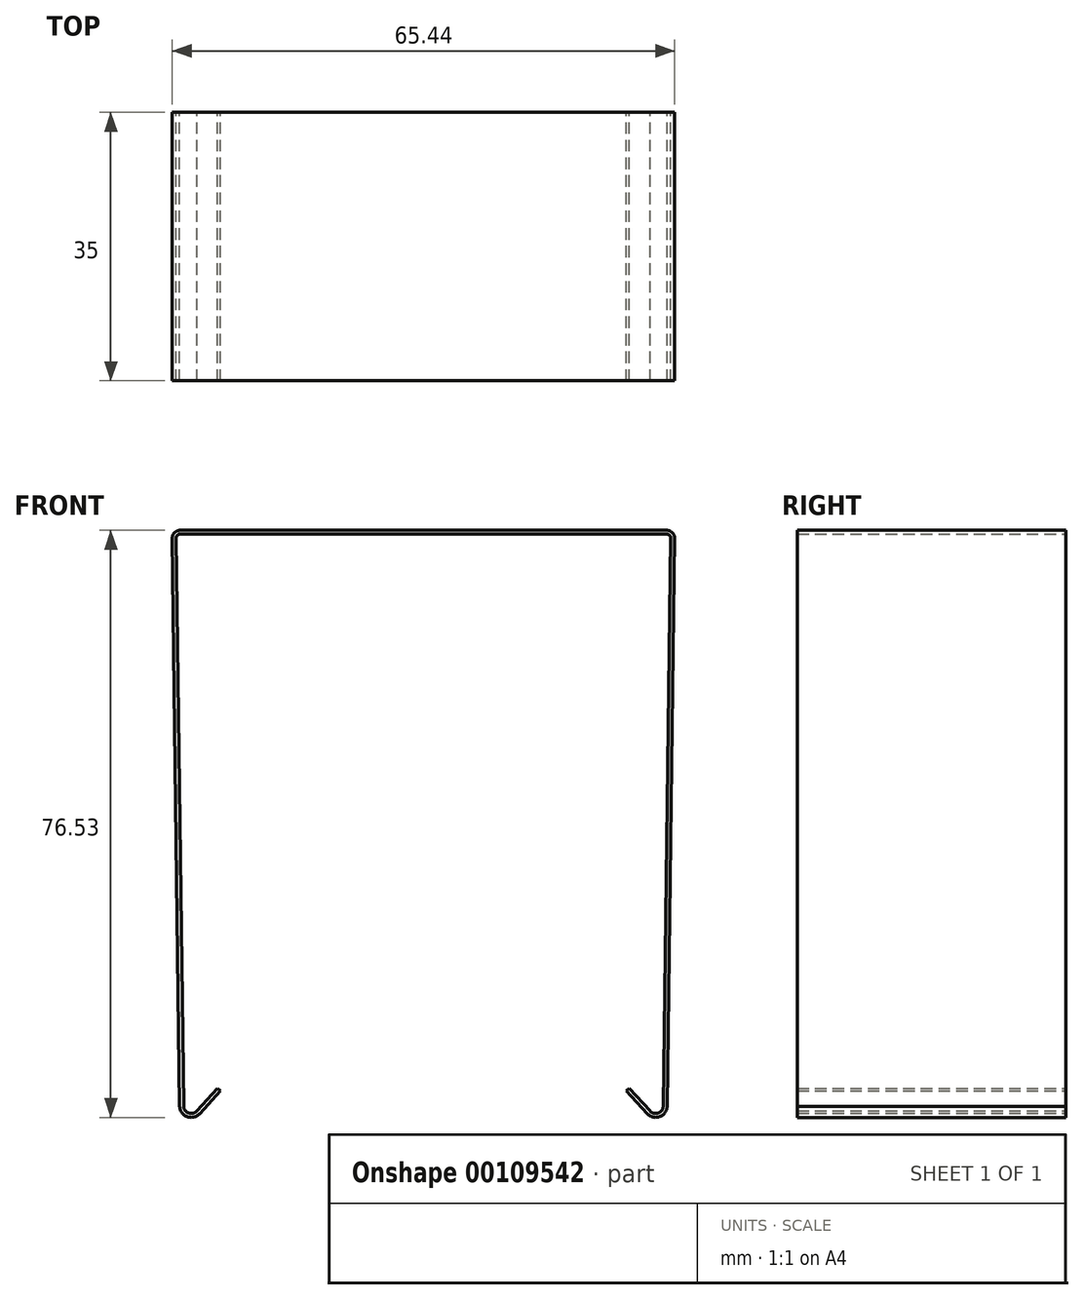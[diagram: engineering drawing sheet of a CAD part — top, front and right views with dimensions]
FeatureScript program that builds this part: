
annotation { "Feature Type Name" : "Feature", "Feature Type Description" : "" }
export const myFeature = defineFeature(function(context is Context, id is Id, definition is map)
    precondition{}
    {
        {
            var Q0;
            Q0=qCreatedBy(makeId("Front.planeOp"),FACE);
            var sketch = newSketch(context, id + "F0", { "sketchPlane" : qUnion([Q0])});
            skLineSegment(sketch, "E0", {"start": v(0, 0) * mm, "end": v(12.09, 0) * mm});
            skLineSegment(sketch, "E1", {"start": v(32.7, -3.05) * mm, "end": v(31.76, -75.1) * mm});
            skLineSegment(sketch, "E2", {"start": v(26.47, -73.06) * mm, "end": v(29.15, -76.03) * mm});
            skArc(sketch, "E3", {"start": v(29.15, -76.03) * mm, "mid": v(30.77, -76.44) * mm, "end": v(31.76, -75.1) * mm});
            skLineSegment(sketch, "E4", {"start": v(26.47, -73.06) * mm, "end": v(26.84, -72.73) * mm});
            skLineSegment(sketch, "E5", {"start": v(26.84, -72.73) * mm, "end": v(29.52, -75.7) * mm});
            skLineSegment(sketch, "E6", {"start": v(31.25, -75.03) * mm, "end": v(32.2, -3.03) * mm});
            skArc(sketch, "E7", {"start": v(29.52, -75.7) * mm, "mid": v(30.61, -75.94) * mm, "end": v(31.25, -75.03) * mm});
            skLineSegment(sketch, "E8", {"start": v(0, 0) * mm, "end": v(0, -0.5) * mm});
            skLineSegment(sketch, "E9", {"start": v(12.09, -0.5) * mm, "end": v(0, -0.5) * mm});
            skLineSegment(sketch, "E10", {"start": v(32.2, -3.03) * mm, "end": v(40.94, -3.03) * mm, "construction": true});
            skLineSegment(sketch, "E11", {"start": v(31.25, -75.03) * mm, "end": v(43.25, -75.03) * mm, "construction": true});
            skLineSegment(sketch, "E12", {"start": v(12.09, 0) * mm, "end": v(31.72, 0) * mm});
            skLineSegment(sketch, "E13", {"start": v(32.7, -3.05) * mm, "end": v(32.72, -1.01) * mm});
            skPoint(sketch, "E14.visualSharp", {"position": v(32.74, 0) * mm});
            skArc(sketch, "E14.filletArc", {"start": v(32.72, -1.01) * mm, "mid": v(32.44, -0.3) * mm, "end": v(31.72, 0) * mm});
            skLineSegment(sketch, "E15", {"start": v(12.09, -0.5) * mm, "end": v(31.72, -0.5) * mm});
            skLineSegment(sketch, "E16", {"start": v(32.2, -3.03) * mm, "end": v(32.22, -1) * mm});
            skPoint(sketch, "E17.visualSharp", {"position": v(32.23, -0.5) * mm});
            skArc(sketch, "E17.filletArc", {"start": v(32.22, -1) * mm, "mid": v(32.08, -0.65) * mm, "end": v(31.72, -0.5) * mm});
            skArc(sketch, "E18.MirrorCS", {"start": v(-29.15, -76.03) * mm, "mid": v(-30.77, -76.44) * mm, "end": v(-31.76, -75.1) * mm});
            skArc(sketch, "E19.MirrorCS", {"start": v(-29.52, -75.7) * mm, "mid": v(-30.61, -75.94) * mm, "end": v(-31.25, -75.03) * mm});
            skArc(sketch, "E20.MirrorCS", {"start": v(-32.72, -1.01) * mm, "mid": v(-32.44, -0.3) * mm, "end": v(-31.72, 0) * mm});
            skLineSegment(sketch, "E21.MirrorCS", {"start": v(-26.47, -73.06) * mm, "end": v(-26.84, -72.73) * mm});
            skArc(sketch, "E22.MirrorCS", {"start": v(-32.22, -1) * mm, "mid": v(-32.08, -0.65) * mm, "end": v(-31.72, -0.5) * mm});
            skLineSegment(sketch, "E23.MirrorCS", {"start": v(-32.7, -3.05) * mm, "end": v(-32.72, -1.01) * mm});
            skLineSegment(sketch, "E24.MirrorCS", {"start": v(-32.2, -3.03) * mm, "end": v(-32.22, -1) * mm});
            skLineSegment(sketch, "E25.MirrorCS", {"start": v(-26.47, -73.06) * mm, "end": v(-29.15, -76.03) * mm});
            skLineSegment(sketch, "E26.MirrorCS", {"start": v(-26.84, -72.73) * mm, "end": v(-29.52, -75.7) * mm});
            skLineSegment(sketch, "E27.MirrorCS", {"start": v(0, 0) * mm, "end": v(-12.09, 0) * mm});
            skLineSegment(sketch, "E28.MirrorCS", {"start": v(-12.09, 0) * mm, "end": v(-31.72, 0) * mm});
            skLineSegment(sketch, "E29.MirrorCS", {"start": v(-12.09, -0.5) * mm, "end": v(0, -0.5) * mm});
            skLineSegment(sketch, "E30.MirrorCS", {"start": v(-31.25, -75.03) * mm, "end": v(-43.25, -75.03) * mm, "construction": true});
            skLineSegment(sketch, "E31.MirrorCS", {"start": v(-32.2, -3.03) * mm, "end": v(-40.94, -3.03) * mm, "construction": true});
            skLineSegment(sketch, "E32.MirrorCS", {"start": v(-12.09, -0.5) * mm, "end": v(-31.72, -0.5) * mm});
            skPoint(sketch, "E33.MirrorP", {"position": v(-32.23, -0.5) * mm});
            skLineSegment(sketch, "E34.MirrorCS", {"start": v(-32.7, -3.05) * mm, "end": v(-31.76, -75.1) * mm});
            skLineSegment(sketch, "E35.MirrorCS", {"start": v(-31.25, -75.03) * mm, "end": v(-32.2, -3.03) * mm});
            skPoint(sketch, "E36.MirrorP", {"position": v(-32.74, 0) * mm});
            skSolve(sketch);
        }
        {
            var Q0;
            Q0=qSketchRegion(id+"F0",true);
            extrude(context, id + "F1", {"entities" : qUnion([Q0]), "depth" : 35 * mm});
        }
    });
